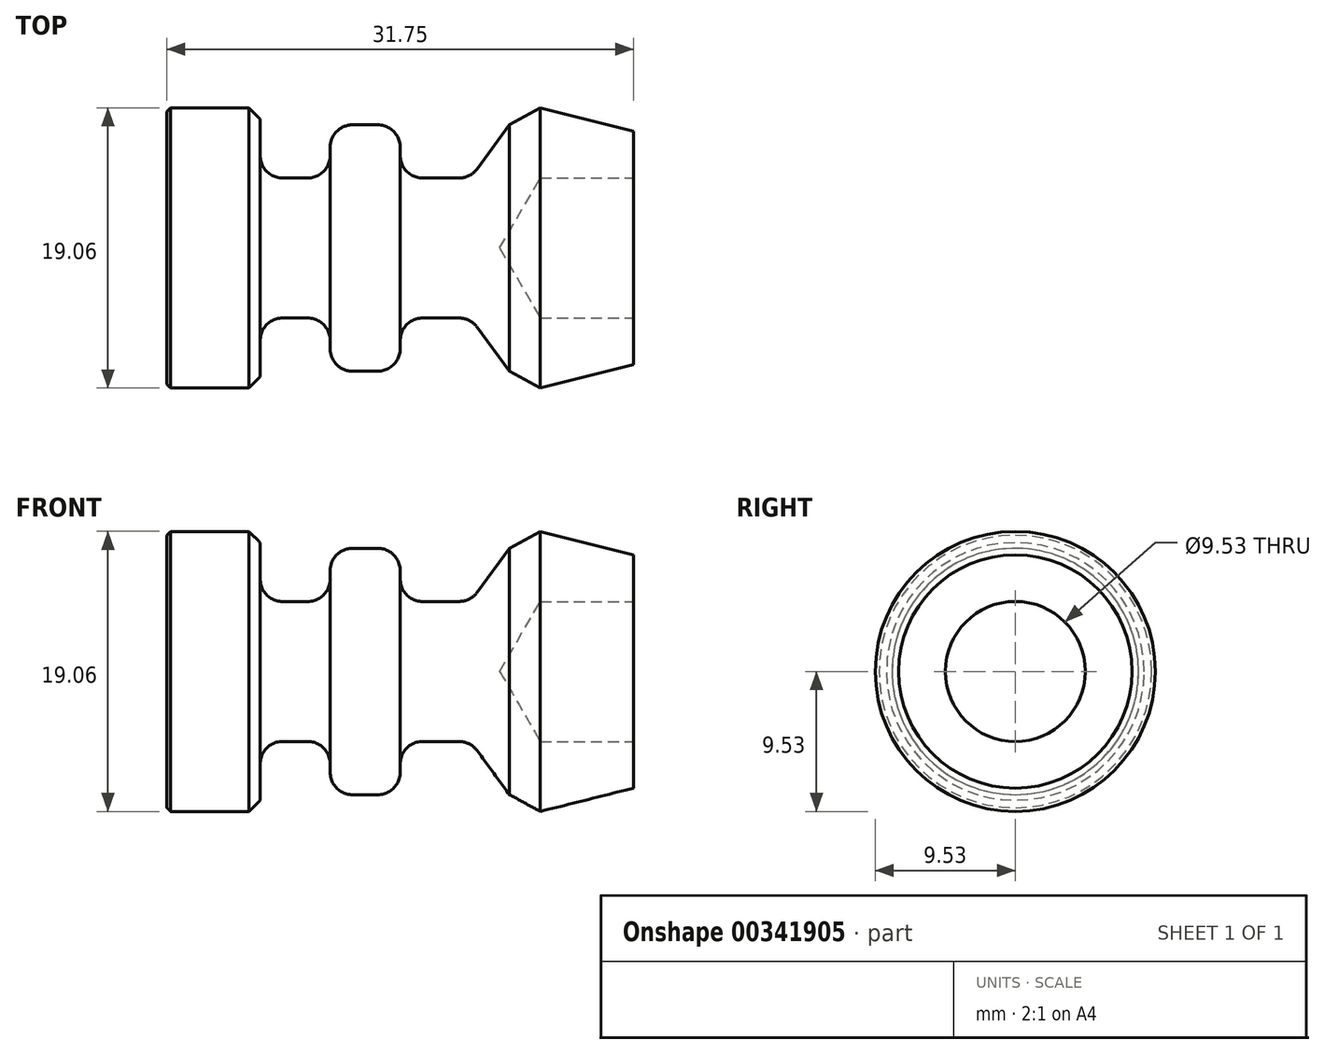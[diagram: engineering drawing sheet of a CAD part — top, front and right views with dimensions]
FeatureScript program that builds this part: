
annotation { "Feature Type Name" : "Feature", "Feature Type Description" : "" }
export const myFeature = defineFeature(function(context is Context, id is Id, definition is map)
    precondition{}
    {
        {
            var Q0;
            Q0=qCreatedBy(makeId("Front.planeOp"),FACE);
            var sketch = newSketch(context, id + "F0", { "sketchPlane" : qUnion([Q0])});
            skLineSegment(sketch, "E0", {"start": v(0, 0) * mm, "end": v(-31.75, 0) * mm});
            skLineSegment(sketch, "E1", {"start": v(-31.75, 0) * mm, "end": v(-31.75, 9.52) * mm});
            skLineSegment(sketch, "E2", {"start": v(-31.75, 9.53) * mm, "end": v(-25.4, 9.53) * mm});
            skLineSegment(sketch, "E3", {"start": v(-25.4, 9.52) * mm, "end": v(-25.4, 4.76) * mm});
            skLineSegment(sketch, "E4", {"start": v(-25.4, 4.76) * mm, "end": v(-20.64, 4.76) * mm});
            skLineSegment(sketch, "E5", {"start": v(-20.64, 4.76) * mm, "end": v(-20.64, 8.38) * mm});
            skLineSegment(sketch, "E6", {"start": v(-20.64, 8.38) * mm, "end": v(-15.88, 8.38) * mm});
            skLineSegment(sketch, "E7", {"start": v(-15.87, 8.38) * mm, "end": v(-15.87, 4.76) * mm});
            skLineSegment(sketch, "E8", {"start": v(-15.88, 4.76) * mm, "end": v(-11.1, 4.76) * mm});
            skLineSegment(sketch, "E9", {"start": v(-11.1, 4.76) * mm, "end": v(-8.43, 8.38) * mm});
            skLineSegment(sketch, "E10", {"start": v(-8.43, 8.38) * mm, "end": v(-6.35, 9.53) * mm});
            skLineSegment(sketch, "E11", {"start": v(-6.35, 9.52) * mm, "end": v(0, 7.94) * mm});
            skLineSegment(sketch, "E12", {"start": v(0, 7.94) * mm, "end": v(0, 4.76) * mm});
            skLineSegment(sketch, "E13", {"start": v(0, 4.76) * mm, "end": v(-6.35, 4.76) * mm});
            skLineSegment(sketch, "E14", {"start": v(-6.35, 4.76) * mm, "end": v(-9.1, 0) * mm});
            skSolve(sketch);
        }
        {
            var Q0;
            {var subQ0=sQuery(id+"F0.wireOp",EDGE,"E1");Q0=makeQuery(id+"F0.imprint","IMPRINT",FACE,{"disambiguationData":[TD([[makeQuery(id+"F0.imprint","IMPRINT",EDGE,{"derivedFrom":subQ0}),-1.0]])]});}
            var Q1;
            Q1=sQuery(id+"F0.wireOp",EDGE,"E0");
            revolve(context, id + "F1", {"entities" : qUnion([Q0]), "axis" : qUnion([Q1]), "revolveType" : RevolveType.FULL});
        }
        {
            var Q0;
            Q0=makeQuery(id+"F1.opRevolve","SWEPT_EDGE",EDGE,{"disambiguationData":[OSD([sQuery(id+"F0.wireOp",EDGE,"E5"),sQuery(id+"F0.wireOp",EDGE,"E6")])]});
            var Q1;
            Q1=makeQuery(id+"F1.opRevolve","SWEPT_EDGE",EDGE,{"disambiguationData":[OSD([sQuery(id+"F0.wireOp",EDGE,"E7"),sQuery(id+"F0.wireOp",EDGE,"E8")])]});
            var Q2;
            Q2=makeQuery(id+"F1.opRevolve","SWEPT_EDGE",EDGE,{"disambiguationData":[OSD([sQuery(id+"F0.wireOp",EDGE,"E6"),sQuery(id+"F0.wireOp",EDGE,"E7")])]});
            var Q3;
            Q3=makeQuery(id+"F1.opRevolve","SWEPT_FACE",FACE,{"disambiguationData":[OSD([sQuery(id+"F0.wireOp",EDGE,"E5")])]});
            var Q4;
            Q4=makeQuery(id+"F1.opRevolve","SWEPT_EDGE",EDGE,{"disambiguationData":[OSD([sQuery(id+"F0.wireOp",EDGE,"E8"),sQuery(id+"F0.wireOp",EDGE,"E9")])]});
            var Q5;
            Q5=makeQuery(id+"F1.opRevolve","SWEPT_EDGE",EDGE,{"disambiguationData":[OSD([sQuery(id+"F0.wireOp",EDGE,"E3"),sQuery(id+"F0.wireOp",EDGE,"E4")])]});
            fillet(context, id + "F2", {"entities" : qUnion([Q0, Q1, Q2, Q3, Q4, Q5]), "radius" : 1.52 * mm, "tangentPropagation" : true, "allowEdgeOverflow" : false});
        }
        {
            var Q0;
            Q0=makeQuery(id+"F1.opRevolve","SWEPT_EDGE",EDGE,{"disambiguationData":[OSD([sQuery(id+"F0.wireOp",EDGE,"E2"),sQuery(id+"F0.wireOp",EDGE,"E3")])]});
            chamfer(context, id + "F3", {"entities" : qUnion([Q0]), "width" : 0.76 * mm, "tangentPropagation" : true});
        }
        {
            var Q0;
            Q0=makeQuery(id+"F1.opRevolve","SWEPT_EDGE",EDGE,{"disambiguationData":[OSD([sQuery(id+"F0.wireOp",EDGE,"E1"),sQuery(id+"F0.wireOp",EDGE,"E2")])]});
            chamfer(context, id + "F4", {"entities" : qUnion([Q0]), "width" : 0.25 * mm, "tangentPropagation" : true});
        }
    });
